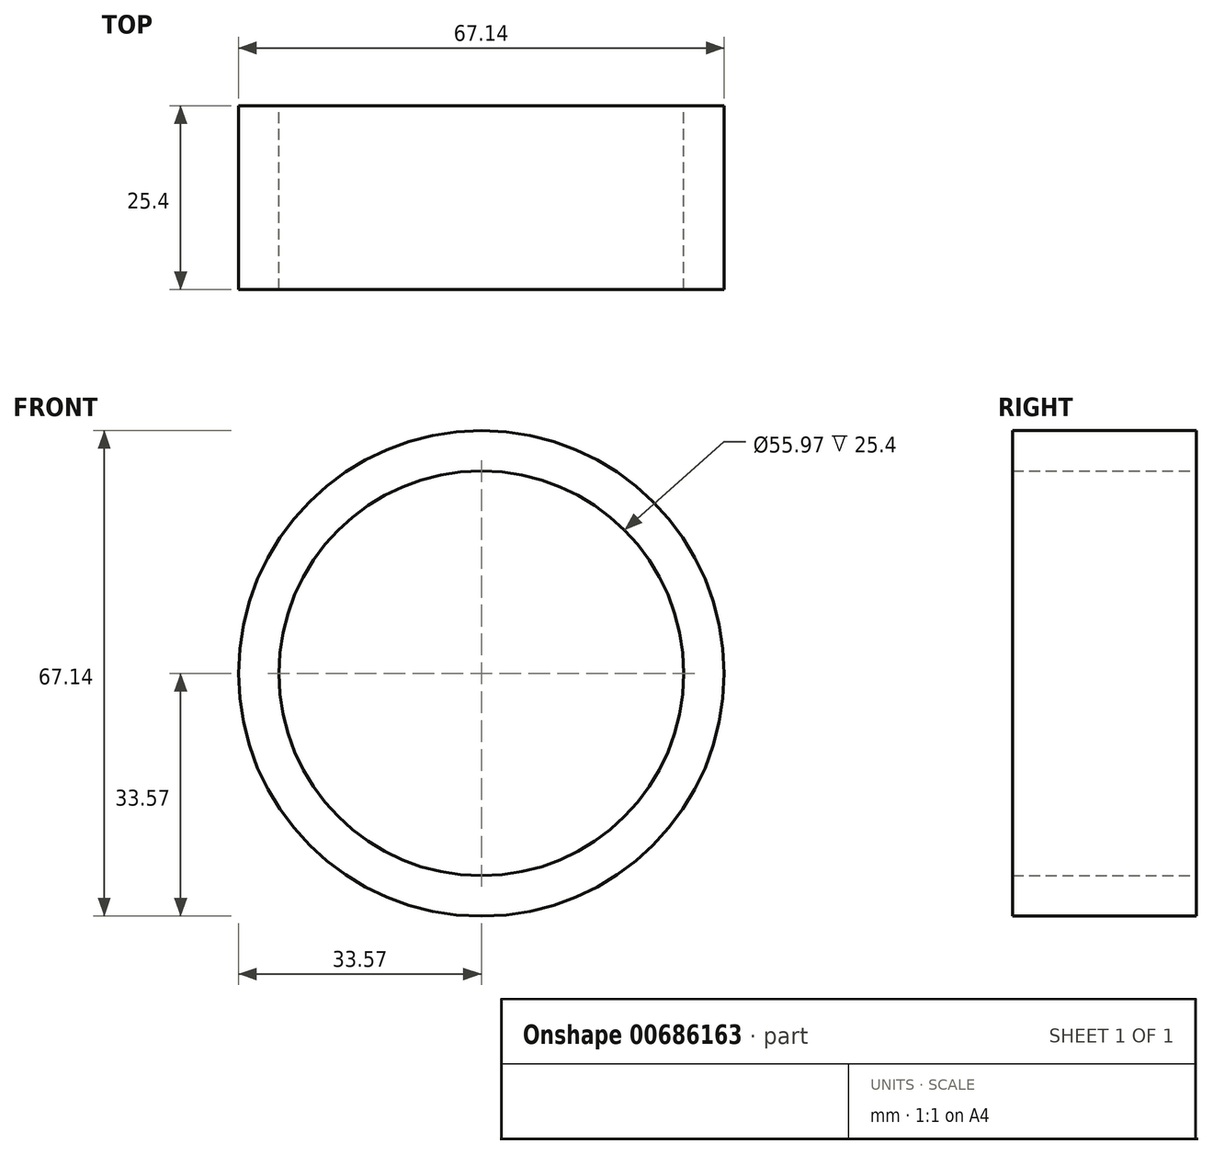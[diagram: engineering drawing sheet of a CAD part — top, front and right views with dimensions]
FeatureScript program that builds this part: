
annotation { "Feature Type Name" : "Feature", "Feature Type Description" : "" }
export const myFeature = defineFeature(function(context is Context, id is Id, definition is map)
    precondition{}
    {
        {
            var Q0;
            Q0=qCreatedBy(makeId("Front.planeOp"),FACE);
            var sketch = newSketch(context, id + "F0", { "sketchPlane" : qUnion([Q0])});
            skCircle(sketch, "E0", {"center": v(0, 0) * mm, "radius": 33.57 * mm});
            skCircle(sketch, "E1.0", {"center": v(0, 0) * mm, "radius": 27.99 * mm});
            skSolve(sketch);
        }
        {
            var Q0;
            Q0 = qSketchRegion(id + "F0", true);
            extrude(context, id + "F1", {"entities" : qUnion([Q0]), "depth" : 25.4 * mm, "offsetDistance" : 25.4 * mm});
        }
    });
